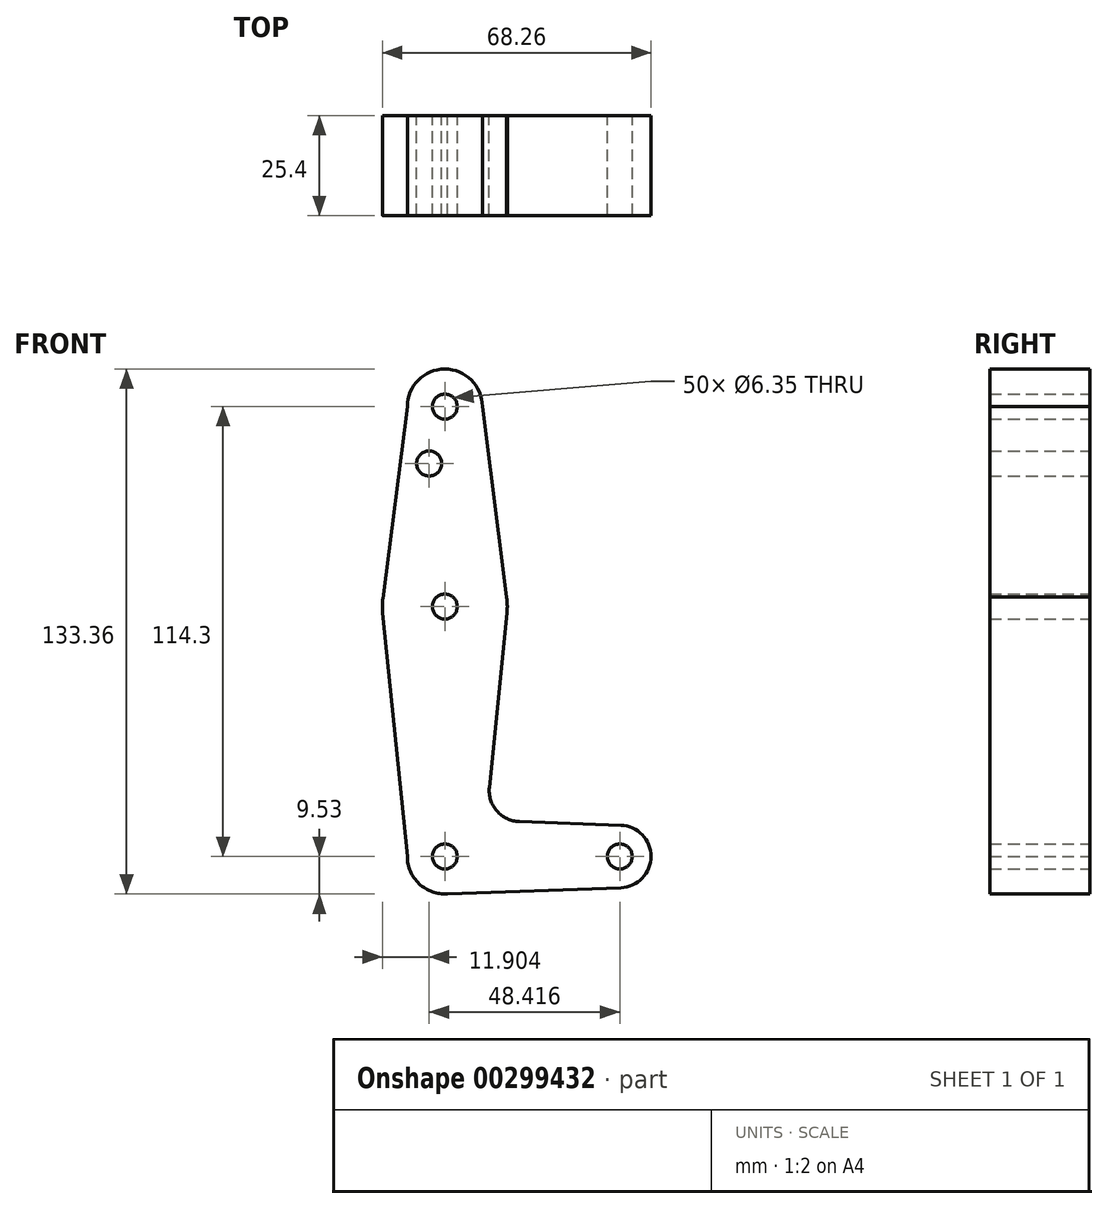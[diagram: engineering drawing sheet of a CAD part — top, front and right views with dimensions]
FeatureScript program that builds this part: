
annotation { "Feature Type Name" : "Feature", "Feature Type Description" : "" }
export const myFeature = defineFeature(function(context is Context, id is Id, definition is map)
    precondition{}
    {
        {
            var Q0;
            Q0=qCreatedBy(makeId("Front.planeOp"),FACE);
            var sketch = newSketch(context, id + "F0", { "sketchPlane" : qUnion([Q0])});
            skLineSegment(sketch, "E0", {"start": v(0, 0) * mm, "end": v(0, 63.5) * mm, "construction": true});
            skLineSegment(sketch, "E1", {"start": v(0, 63.5) * mm, "end": v(0, 114.3) * mm, "construction": true});
            skLineSegment(sketch, "E2", {"start": v(0, 0) * mm, "end": v(44.45, 0) * mm, "construction": true});
            skCircle(sketch, "E3", {"center": v(0, 0) * mm, "radius": 9.53 * mm});
            skCircle(sketch, "E4", {"center": v(0, 63.5) * mm, "radius": 15.88 * mm});
            skCircle(sketch, "E5", {"center": v(0, 114.3) * mm, "radius": 9.53 * mm});
            skCircle(sketch, "E6", {"center": v(44.45, 0) * mm, "radius": 7.94 * mm});
            skLineSegment(sketch, "E7", {"start": v(0, -9.53) * mm, "end": v(44.73, -7.93) * mm});
            skLineSegment(sketch, "E8", {"start": v(18.93, 8.85) * mm, "end": v(44.73, 7.93) * mm});
            skLineSegment(sketch, "E9", {"start": v(-9.53, 0) * mm, "end": v(-15.8, 61.9) * mm});
            skLineSegment(sketch, "E10", {"start": v(11.3, 17.6) * mm, "end": v(15.8, 61.9) * mm});
            skLineSegment(sketch, "E11", {"start": v(-9.53, 114.3) * mm, "end": v(-15.75, 65.5) * mm});
            skLineSegment(sketch, "E12", {"start": v(9.53, 114.3) * mm, "end": v(15.8, 65.1) * mm});
            skCircle(sketch, "E13", {"center": v(0, 114.3) * mm, "radius": 3.18 * mm});
            skCircle(sketch, "E14", {"center": v(0, 63.5) * mm, "radius": 3.18 * mm});
            skCircle(sketch, "E15", {"center": v(0, 0) * mm, "radius": 3.18 * mm});
            skCircle(sketch, "E16", {"center": v(44.45, 0) * mm, "radius": 3.18 * mm});
            skArc(sketch, "E17.filletArc", {"start": v(11.3, 17.6) * mm, "mid": v(13.22, 11.57) * mm, "end": v(18.93, 8.85) * mm});
            skCircle(sketch, "E18", {"center": v(-3.97, 99.85) * mm, "radius": 3.18 * mm});
            skSolve(sketch);
        }
        {
            var Q0;
            Q0 = qSketchRegion(id + "F0", true);
            extrude(context, id + "F1", {"entities" : qUnion([Q0]), "depth" : 25.4 * mm});
        }
    });
